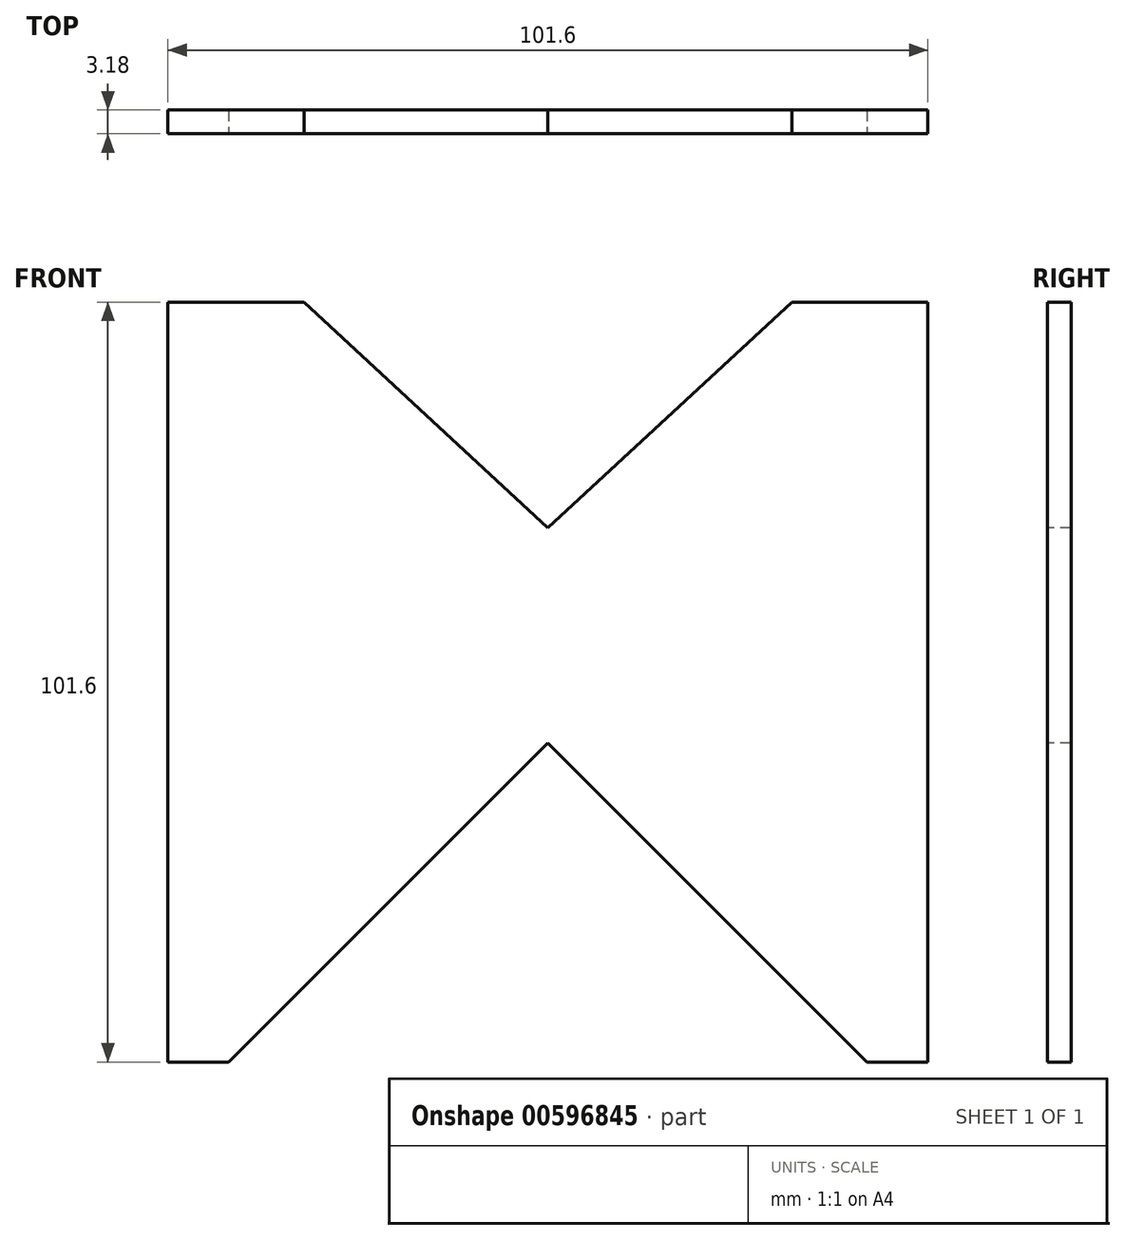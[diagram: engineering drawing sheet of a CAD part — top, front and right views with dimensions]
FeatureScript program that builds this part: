
annotation { "Feature Type Name" : "Feature", "Feature Type Description" : "" }
export const myFeature = defineFeature(function(context is Context, id is Id, definition is map)
    precondition{}
    {
        {
            var Q0;
            Q0=qCreatedBy(makeId("Front.planeOp"),FACE);
            var sketch = newSketch(context, id + "F0", { "sketchPlane" : qUnion([Q0])});
            skLineSegment(sketch, "E0.bottom", {"start": v(-50.8, 50.8) * mm, "end": v(50.8, 50.8) * mm});
            skLineSegment(sketch, "E0.top", {"start": v(-50.8, -50.8) * mm, "end": v(50.8, -50.8) * mm});
            skLineSegment(sketch, "E0.left", {"start": v(-50.8, 50.8) * mm, "end": v(-50.8, -50.8) * mm});
            skLineSegment(sketch, "E0.right", {"start": v(50.8, 50.8) * mm, "end": v(50.8, -50.8) * mm});
            skPoint(sketch, "E0.middle", {"position": v(0, 0) * mm});
            skSolve(sketch);
        }
        {
            var Q0;
            Q0=makeQuery(id+"F0.imprint","IMPRINT",FACE,{"disambiguationData":[TD([[makeQuery(id+"F0.imprint","IMPRINT",EDGE,{"derivedFrom":sQuery(id+"F0.wireOp",EDGE,"E0.bottom")}),-1.0]])]});
            extrude(context, id + "F1", {"entities" : qUnion([Q0]), "depth" : 3.17 * mm, "offsetDistance" : 25.4 * mm});
        }
        {
            var Q0;
            Q0=makeQuery(id+"F1.opExtrude","CAP_FACE",FACE,{"disambiguationData":[OSD([sQuery(id+"F0.wireOp",EDGE,"E0.bottom"),sQuery(id+"F0.wireOp",EDGE,"E0.top"),sQuery(id+"F0.wireOp",EDGE,"E0.left"),sQuery(id+"F0.wireOp",EDGE,"E0.right")])],"isStart":false});
            var sketch = newSketch(context, id + "F2", { "sketchPlane" : qUnion([Q0])});
            skLineSegment(sketch, "E1", {"start": v(-32.6, 50.8) * mm, "end": v(0, 20.58) * mm});
            skLineSegment(sketch, "E2", {"start": v(0, 20.58) * mm, "end": v(32.6, 50.8) * mm});
            skLineSegment(sketch, "E3", {"start": v(32.6, 50.8) * mm, "end": v(-32.6, 50.8) * mm});
            skSolve(sketch);
        }
        {
            var Q0;
            Q0=makeQuery(id+"F2.imprint","IMPRINT",FACE,{"disambiguationData":[TD([[makeQuery(id+"F2.imprint","IMPRINT",EDGE,{"derivedFrom":sQuery(id+"F2.wireOp",EDGE,"E1")}),1.0]])]});
            extrude(context, id + "F3", {"entities" : qUnion([Q0]), "operationType" : NewBodyOperationType.REMOVE, "endBound" : BoundingType.THROUGH_ALL, "oppositeDirection" : true, "depth" : 25.4 * mm, "offsetDistance" : 25.4 * mm});
        }
        {
            var Q0;
            Q0=makeQuery(id+"F1.opExtrude","CAP_FACE",FACE,{"disambiguationData":[OSD([sQuery(id+"F0.wireOp",EDGE,"E0.bottom"),sQuery(id+"F0.wireOp",EDGE,"E0.top"),sQuery(id+"F0.wireOp",EDGE,"E0.left"),sQuery(id+"F0.wireOp",EDGE,"E0.right")])],"isStart":false});
            var sketch = newSketch(context, id + "F4", { "sketchPlane" : qUnion([Q0])});
            skLineSegment(sketch, "E4", {"start": v(-42.66, -50.8) * mm, "end": v(0, -8.14) * mm});
            skLineSegment(sketch, "E5", {"start": v(0, -8.14) * mm, "end": v(42.66, -50.8) * mm});
            skLineSegment(sketch, "E6", {"start": v(42.66, -50.8) * mm, "end": v(-42.66, -50.8) * mm});
            skSolve(sketch);
        }
        {
            var Q0;
            Q0=makeQuery(id+"F4.imprint","IMPRINT",FACE,{"disambiguationData":[TD([[makeQuery(id+"F4.imprint","IMPRINT",EDGE,{"derivedFrom":sQuery(id+"F4.wireOp",EDGE,"E4")}),-1.0]])]});
            extrude(context, id + "F5", {"entities" : qUnion([Q0]), "operationType" : NewBodyOperationType.REMOVE, "oppositeDirection" : true, "depth" : 25.4 * mm, "offsetDistance" : 25.4 * mm});
        }
    });
